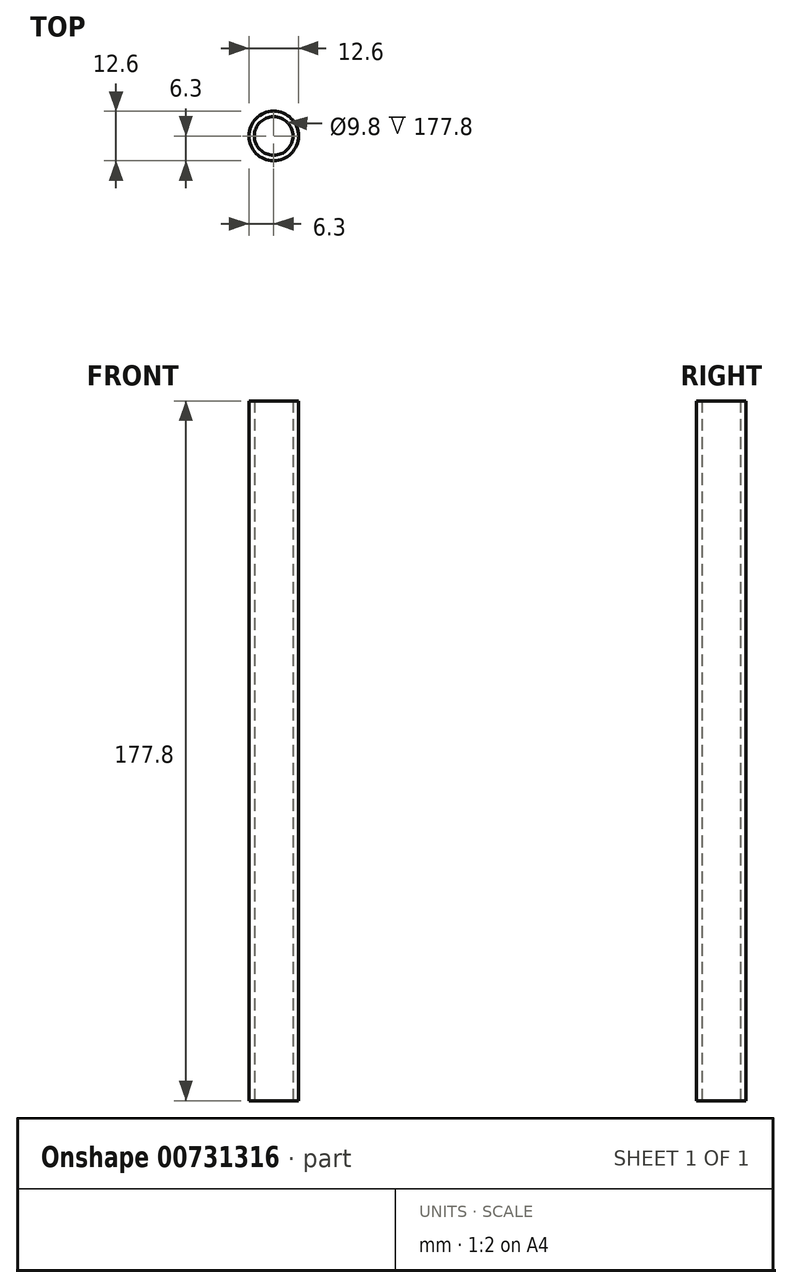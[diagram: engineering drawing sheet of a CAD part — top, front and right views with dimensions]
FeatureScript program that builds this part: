
annotation { "Feature Type Name" : "Feature", "Feature Type Description" : "" }
export const myFeature = defineFeature(function(context is Context, id is Id, definition is map)
    precondition{}
    {
        {
            var Q0;
            Q0=qCreatedBy(makeId("Top.planeOp"),FACE);
            var sketch = newSketch(context, id + "F0", { "sketchPlane" : qUnion([Q0])});
            skCircle(sketch, "E0", {"center": v(0, 0) * mm, "radius": 6.3 * mm});
            skCircle(sketch, "E1", {"center": v(0, 0) * mm, "radius": 4.9 * mm});
            skSolve(sketch);
        }
        {
            var Q0;
            Q0=makeQuery(id+"F0.imprint","IMPRINT",FACE,{"disambiguationData":[TD([[makeQuery(id+"F0.imprint","IMPRINT",EDGE,{"derivedFrom":sQuery(id+"F0.wireOp",EDGE,"E0")}),1.0]])]});
            extrude(context, id + "F1", {"entities" : qUnion([Q0]), "depth" : 177.8 * mm, "offsetDistance" : 25.4 * mm});
        }
    });
